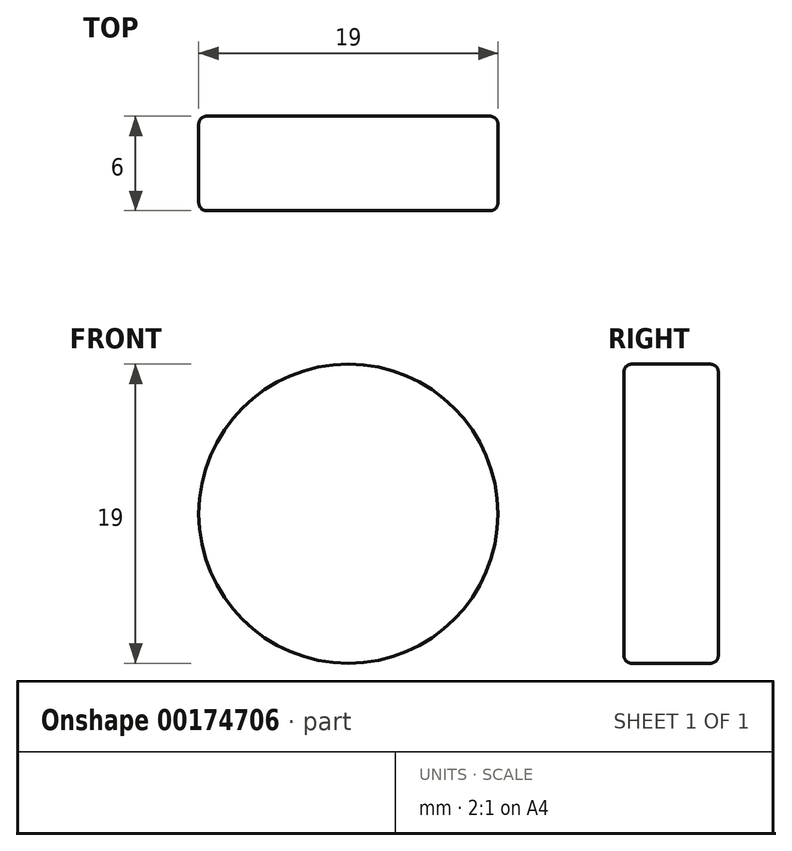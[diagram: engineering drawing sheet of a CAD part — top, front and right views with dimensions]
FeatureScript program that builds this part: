
annotation { "Feature Type Name" : "Feature", "Feature Type Description" : "" }
export const myFeature = defineFeature(function(context is Context, id is Id, definition is map)
    precondition{}
    {
        {
            var Q0;
            Q0=qCreatedBy(makeId("Front.planeOp"),FACE);
            var sketch = newSketch(context, id + "F0", { "sketchPlane" : qUnion([Q0])});
            skCircle(sketch, "E0", {"center": v(0, 0) * mm, "radius": 9.5 * mm});
            skSolve(sketch);
        }
        {
            var Q0;
            Q0=makeQuery(id+"F0.imprint","IMPRINT",FACE,{"disambiguationData":[TD([[makeQuery(id+"F0.imprint","IMPRINT",EDGE,{"derivedFrom":sQuery(id+"F0.wireOp",EDGE,"E0")}),1.0]])]});
            extrude(context, id + "F1", {"entities" : qUnion([Q0]), "depth" : 6 * mm});
        }
        {
            var Q0;
            Q0=makeQuery(id+"F1.opExtrude","CAP_EDGE",EDGE,{"disambiguationData":[OSD([sQuery(id+"F0.wireOp",EDGE,"E0")])],"isStart":false});
            var Q1;
            Q1=makeQuery(id+"F1.opExtrude","SWEPT_FACE",FACE,{"disambiguationData":[OSD([sQuery(id+"F0.wireOp",EDGE,"E0")])]});
            fillet(context, id + "F2", {"entities" : qUnion([Q0, Q1]), "radius" : 0.5 * mm, "tangentPropagation" : true, "allowEdgeOverflow" : false});
        }
    });
